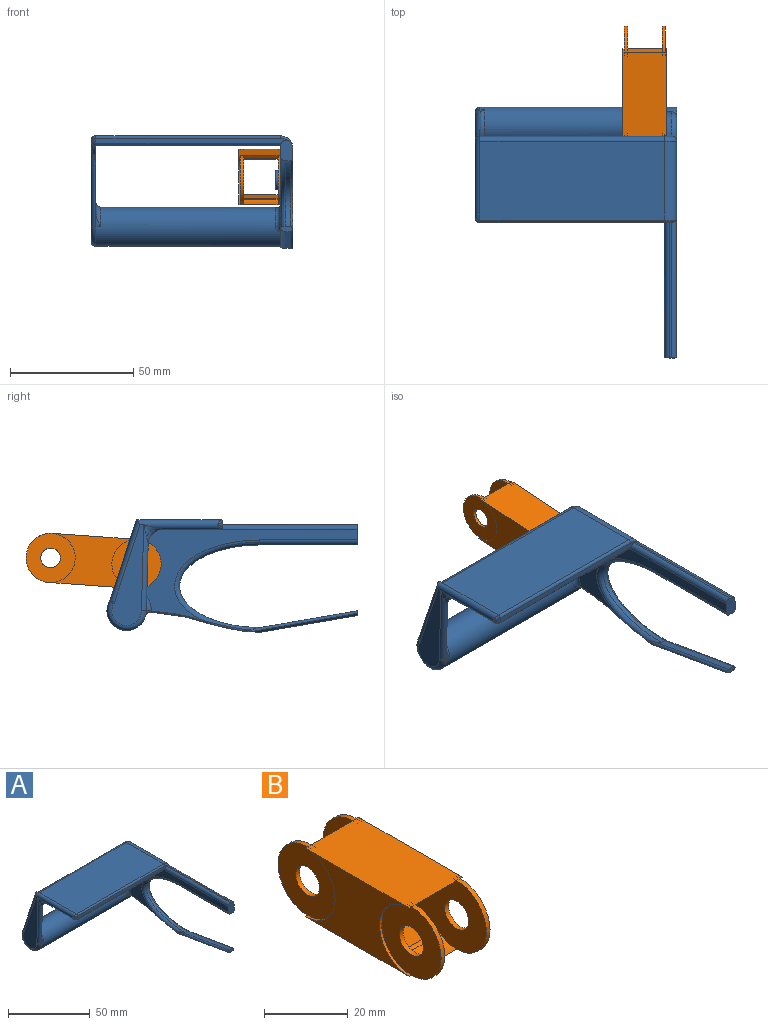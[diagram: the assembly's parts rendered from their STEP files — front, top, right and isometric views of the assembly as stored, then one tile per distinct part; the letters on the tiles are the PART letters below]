
ASSEMBLY  parts=2 mates=1
PART A: 63 faces, bbox 84.6x105.6x47.5 mm
  f0: plane 100x38.71mm, normal (-1,0,0), area 1065.4mm2, adj f1,f3,f11,f12,f15,f22,f25,f27
  f1: plane 6x3mm, normal (0,1,0), area 16.1mm2, adj f0,f27,f47,f48
  f2: plane 55.01x0.83mm, normal (0,0,1), area 45.6mm2, adj f3,f21,f25,f26,f51
  f3: plane 8.23x5mm, normal (0,-1,0), area 38mm2, adj f0,f2,f4,f10,f12,f19,f24,f25
  f4: plane 40x2mm, normal (0,0,-1), area 80mm2, adj f3,f5,f12,f19
  f5: extruded ~33.55x33.12mm, area 160mm2, adj f4,f6,f11,f18
  f6: plane 41.35x7.47mm, normal (0,0.17,0.99), area 120.4mm2, adj f5,f7,f11,f13,f17
  f7: plane 5.07x2mm, normal (0,-1,0), area 8.4mm2, adj f6,f8,f13,f14,f17,f20
  f8: plane 39.48x6.79mm, normal (0,-0.17,-0.99), area 74.5mm2, adj f7,f9,f14,f20
  f9: extruded ~44.65x8.15mm, area 199.3mm2, adj f8,f10,f13,f14,f15,f16,f20,f56
  f10: plane 102.61x41.22mm, normal (1,0,0), area 1305.1mm2, adj f3,f9,f18,f19,f20,f24,f30,f31
  f11: bspline ~37.55x35.12mm, area 241.8mm2, adj f0,f5,f6,f12,f13,f16
  f12: cylinder r=2mm len=40mm, axis (0,1,0), area 125.7mm2, adj f0,f3,f4,f11
  f13: cylinder r=1mm len=47.33mm, axis (0,-0.99,0.17), area 68.5mm2, adj f6,f7,f9,f11,f14,f16
  f14: cylinder r=3mm len=43.78mm, axis (0,-0.99,0.17), area 100.6mm2, adj f7,f8,f9,f13
  f15: bspline ~26.02x5.26mm, area 16.1mm2, adj f0,f9,f16,f55
  f16: bspline ~22.92x5mm, area 19.2mm2, adj f9,f11,f13,f15
  f17: cylinder r=1mm len=39.61mm, axis (0,0.99,-0.17), area 60.7mm2, adj f6,f7,f18,f20
  f18: bspline ~35.55x34.19mm, area 127.5mm2, adj f5,f10,f17,f19,f20
  f19: cylinder r=1mm len=40mm, axis (0,-1,0), area 62.8mm2, adj f3,f4,f10,f18
  f20: cylinder r=1mm len=44.21mm, axis (0,-0.99,0.17), area 64.5mm2, adj f7,f8,f9,f10,f17,f18
  f21: plane 77.65x2mm, normal (0,-1,0), area 152.6mm2, adj f2,f25,f41,f50,f51,f52
  f22: plane 75x32mm, normal (0,0,-1), area 2400mm2, adj f0,f35,f40,f46,f52
  f23: plane 75x32mm, normal (0,0,1), area 2400mm2, adj f24,f40,f46,f50
  f24: cylinder r=5mm len=88mm, axis (0,-1,0), area 346.5mm2, adj f3,f10,f23,f26,f47,f51
  f25: cylinder r=2mm len=56mm, axis (0,-1,0), area 173.3mm2, adj f0,f2,f3,f21,f52
  f26: cylinder r=2mm len=56mm, axis (0,-1,0), area 136.6mm2, adj f2,f3,f24,f51
  f27: cylinder r=10mm len=20mm, axis (-1,0,0), area 94.3mm2, adj f0,f1,f54,f57,f60
  f28: cylinder r=4mm len=8mm, axis (1,0,0), area 50.3mm2, adj f0,f29
  f29: plane 8x8mm, normal (-1,0,0), area 50.3mm2, adj f28
  f30: cylinder r=8mm len=80mm, axis (1,0,0), area 3891.6mm2, adj f10,f36,f37,f38,f43,f54,f55,f56
  f31: cylinder r=2mm len=3.25mm, axis (0,0,-1), area 2.3mm2, adj f10,f58,f59,f60
  f32: plane 5.76x1.95mm, normal (0,-1,-0.03), area 4.1mm2, adj f36,f38,f44
  f33: plane 4.18x1.6mm, normal (0,0.95,0.31), area 2.3mm2, adj f36,f37,f39
  f34: plane 41x12.95mm, normal (-1,0,0), area 295.6mm2, adj f39,f40,f42,f43,f44,f45
  f35: plane 31.39x20.4mm, normal (1,0,0), area 248mm2, adj f22,f36,f39,f40,f44,f46,f62
  f36: torus R=10mm, axis (-1,0,0), area 56.1mm2, adj f30,f32,f33,f35,f37,f38
  f37: cylinder r=2mm len=2mm, axis (1,0,0), area 0.7mm2, adj f30,f33,f36,f42
  f38: cylinder r=2mm len=2mm, axis (1,0,0), area 0.1mm2, adj f30,f32,f36,f45
  f39: cylinder r=2mm len=33.45mm, axis (0,-0.31,0.95), area 106.3mm2, adj f33,f34,f35,f40,f42
  f40: cylinder r=2mm len=34mm, axis (0,-1,0), area 184.4mm2, adj f22,f23,f34,f35,f39,f49,f53,f61
  f41: cylinder r=2mm len=2mm, axis (0,0,-1), area 3.1mm2, adj f21,f49,f53
  f42: torus R=4mm, axis (-1,0,0), area 1.6mm2, adj f34,f37,f39,f43
  f43: torus R=6mm, axis (-1,0,0), area 83.2mm2, adj f30,f34,f42,f45
  f44: cylinder r=2mm len=34.97mm, axis (0,0.03,-1), area 95.2mm2, adj f32,f34,f35,f45,f61,f62
  f45: torus R=4mm, axis (-1,0,0), area 0.2mm2, adj f34,f38,f43,f44
  f46: cylinder r=2mm len=75mm, axis (-1,0,0), area 471.2mm2, adj f0,f22,f23,f35,f47
  f47: torus R=3mm, axis (0,-1,0), area 21.1mm2, adj f1,f24,f46,f48
  f48: cylinder r=2mm len=5.25mm, axis (0,0,-1), area 13mm2, adj f1,f10,f47,f60
  f49: bspline ~2.39x2mm, area 2.2mm2, adj f40,f41,f50
  f50: cylinder r=1mm len=75mm, axis (1,0,0), area 117.8mm2, adj f21,f23,f49,f51
  f51: torus R=4mm, axis (0,1,0), area 7.2mm2, adj f2,f21,f24,f26,f50
  f52: cylinder r=1mm len=75.27mm, axis (-1,0,0), area 118mm2, adj f21,f22,f25,f53
  f53: bspline ~2.39x2mm, area 2.2mm2, adj f40,f41,f52
  f54: torus R=10mm, axis (1,0,0), area 35.4mm2, adj f0,f27,f30,f55,f57
  f55: bspline ~3.05x2.43mm, area 5.2mm2, adj f15,f30,f54,f56
  f56: cylinder r=2mm len=4.5mm, axis (-1,0,0), area 12.7mm2, adj f9,f10,f30,f55
  f57: cylinder r=2mm len=5mm, axis (1,0,0), area 11.2mm2, adj f27,f30,f54,f58
  f58: bspline ~3.69x3.57mm, area 7.1mm2, adj f10,f30,f31,f57,f59,f60
  f59: bspline ~3.34x3.16mm, area 0.8mm2, adj f10,f31,f58
  f60: torus R=8mm, axis (1,0,0), area 97.7mm2, adj f10,f27,f31,f48,f58
  f61: bspline ~5.2x5.16mm, area 6.7mm2, adj f40,f44,f62
  f62: bspline ~6.7x6.63mm, area 15.4mm2, adj f35,f40,f44,f61
PART B: 30 faces, bbox 18x55x20 mm
  f0: plane 1.25x0.03mm, normal (0,1,0), area 0mm2, adj f5,f10,f25,f26
  f1: cylinder r=10mm len=20mm, axis (-1,0,0), area 23.6mm2, adj f11,f12,f13,f29
  f2: plane 35x20mm, normal (-1,0,0), area 385.8mm2, adj f3,f4,f11,f13
  f3: cylinder r=10mm len=20mm, axis (-1,0,0), area 23.6mm2, adj f2,f11,f13,f23
  f4: cylinder r=10mm len=20mm, axis (-1,0,0), area 23.6mm2, adj f2,f11,f13,f20
  f5: plane 54.97x20mm, normal (-1,0,0), area 805.2mm2, adj f0,f6,f8,f9,f14,f15,f16,f17
  f6: plane 1.25x0.03mm, normal (0,1,0), area 0mm2, adj f5,f10,f25,f26
  f7: plane 55x20mm, normal (1,0,0), area 806.4mm2, adj f8,f9,f10,f14,f15,f16,f17,f18
  f8: plane 22.37x14mm, normal (0,0,-1), area 313.1mm2, adj f5,f7,f10,f17
  f9: cylinder r=10mm len=14mm, axis (-1,0,0), area 82mm2, adj f5,f7,f11,f17
  f10: cylinder r=10mm len=20mm, axis (-1,0,0), area 219.8mm2, adj f0,f6,f7,f8,f11,f12,f13,f14
  f11: plane 35x18mm, normal (0,0,1), area 630mm2, adj f1,f2,f3,f4,f9,f10,f12,f18
  f12: plane 35x20mm, normal (1,0,0), area 385.8mm2, adj f1,f10,f11,f13
  f13: plane 35x18mm, normal (0,0,-1), area 630mm2, adj f1,f2,f3,f4,f10,f12,f15,f18
  f14: plane 22.37x14mm, normal (0,0,1), area 313.1mm2, adj f5,f7,f10,f16
  f15: cylinder r=10mm len=14mm, axis (-1,0,0), area 82mm2, adj f5,f7,f13,f16
  f16: cylinder r=2mm len=14mm, axis (-1,0,0), area 16.4mm2, adj f5,f7,f14,f15
  f17: cylinder r=2mm len=14mm, axis (-1,0,0), area 16.4mm2, adj f5,f7,f8,f9
  f18: cylinder r=10mm len=20mm, axis (1,0,0), area 39.3mm2, adj f7,f11,f13,f20
  f19: cylinder r=4mm len=8mm, axis (1,0,0), area 31.4mm2, adj f7,f20
  f20: plane 20x20mm, normal (-1,0,0), area 263.9mm2, adj f4,f18,f19
  f21: cylinder r=10mm len=20mm, axis (1,0,0), area 39.3mm2, adj f7,f11,f13,f23
  f22: cylinder r=4mm len=8mm, axis (1,0,0), area 31.4mm2, adj f7,f23
  f23: plane 20x20mm, normal (-1,0,0), area 263.9mm2, adj f3,f21,f22
  f24: cylinder r=4mm len=8mm, axis (-1,0,0), area 31.4mm2, adj f5,f26
  f25: cylinder r=9.97mm len=19.95mm, axis (-1,0,0), area 55.3mm2, adj f0,f5,f6,f26
  f26: plane 19.97x19.95mm, normal (1,0,0), area 262.7mm2, adj f0,f6,f10,f24,f25
  f27: cylinder r=10mm len=20mm, axis (-1,0,0), area 39.3mm2, adj f5,f11,f13,f29
  f28: cylinder r=4mm len=8mm, axis (-1,0,0), area 31.4mm2, adj f5,f29
  f29: plane 20x20mm, normal (1,0,0), area 263.9mm2, adj f1,f27,f28
PLACE A t=(-3,0,-32)mm
PLACE B rot(axis=(1,0,0),4.1deg) t=(-20,34.91,-10.52)mm
MATE revolute A.f27 <-> B.f1  axis (-1,0,0) through (-5,0,-13)mm
